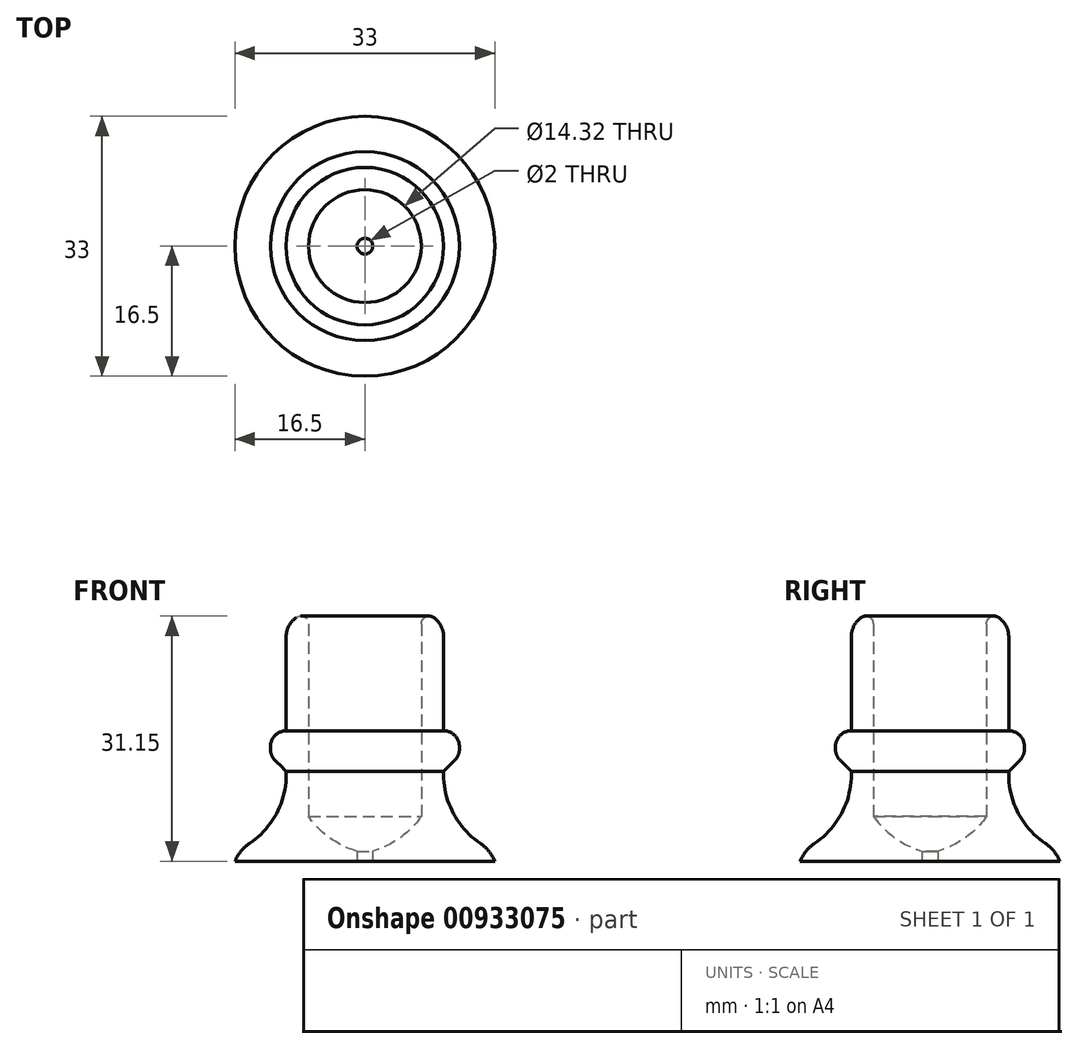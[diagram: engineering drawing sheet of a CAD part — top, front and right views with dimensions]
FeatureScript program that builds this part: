
annotation { "Feature Type Name" : "Feature", "Feature Type Description" : "" }
export const myFeature = defineFeature(function(context is Context, id is Id, definition is map)
    precondition{}
    {
        {
            var Q0;
            Q0=qCreatedBy(makeId("Front.planeOp"),FACE);
            var sketch = newSketch(context, id + "F0", { "sketchPlane" : qUnion([Q0])});
            skLineSegment(sketch, "E0", {"start": v(10, 11.44) * mm, "end": v(12, 13.4) * mm});
            skLineSegment(sketch, "E1", {"start": v(12, 13.4) * mm, "end": v(12, 16.58) * mm});
            skLineSegment(sketch, "E2", {"start": v(0, 0) * mm, "end": v(0, 38.4) * mm, "construction": true});
            skLineSegment(sketch, "E3", {"start": v(12, 16.58) * mm, "end": v(10, 16.58) * mm});
            skLineSegment(sketch, "E4", {"start": v(10, 16.58) * mm, "end": v(10, 31.51) * mm});
            skLineSegment(sketch, "E5", {"start": v(16.5, 0) * mm, "end": v(16.5, 1.28) * mm});
            skArc(sketch, "E6", {"start": v(10, 11.44) * mm, "mid": v(11.66, 5.34) * mm, "end": v(16.5, 1.28) * mm});
            skLineSegment(sketch, "E7", {"start": v(10, 31.51) * mm, "end": v(7.16, 31.51) * mm});
            skLineSegment(sketch, "E8", {"start": v(7.16, 31.51) * mm, "end": v(7.16, 5.7) * mm});
            skLineSegment(sketch, "E9", {"start": v(1, 0.05) * mm, "end": v(1, 1.28) * mm});
            skLineSegment(sketch, "E10", {"start": v(1, 0.05) * mm, "end": v(16.5, 0) * mm});
            skArc(sketch, "E11", {"start": v(1, 1.28) * mm, "mid": v(4.45, 2.97) * mm, "end": v(7.16, 5.7) * mm});
            skSolve(sketch);
        }
        {
            var Q0;
            Q0=makeQuery(id+"F0.imprint","IMPRINT",FACE,{"disambiguationData":[TD([[makeQuery(id+"F0.imprint","IMPRINT",EDGE,{"derivedFrom":sQuery(id+"F0.wireOp",EDGE,"E0")}),1.0]])]});
            var Q1;
            Q1=sQuery(id+"F0.wireOp",EDGE,"E2");
            revolve(context, id + "F1", {"surfaceOperationType" : NewSurfaceOperationType.NEW, "entities" : qUnion([Q0]), "axis" : qUnion([Q1]), "revolveType" : RevolveType.FULL});
        }
        {
            var Q0;
            Q0=makeQuery(id+"F1.opRevolve","SWEPT_EDGE",EDGE,{"disambiguationData":[OSD([sQuery(id+"F0.wireOp",EDGE,"E5"),sQuery(id+"F0.wireOp",EDGE,"E6")])]});
            fillet(context, id + "F2", {"entities" : qUnion([Q0]), "radius" : 5 * mm, "tangentPropagation" : true, "allowEdgeOverflow" : false});
        }
        {
            var Q0;
            Q0=makeQuery(id+"F1.opRevolve","SWEPT_EDGE",EDGE,{"disambiguationData":[OSD([sQuery(id+"F0.wireOp",EDGE,"E0"),sQuery(id+"F0.wireOp",EDGE,"E1")])]});
            fillet(context, id + "F3", {"entities" : qUnion([Q0]), "radius" : 2 * mm, "tangentPropagation" : true, "allowEdgeOverflow" : false});
        }
        {
            var Q0;
            Q0=makeQuery(id+"F1.opRevolve","SWEPT_EDGE",EDGE,{"disambiguationData":[OSD([sQuery(id+"F0.wireOp",EDGE,"E1"),sQuery(id+"F0.wireOp",EDGE,"E3")])]});
            fillet(context, id + "F4", {"entities" : qUnion([Q0]), "radius" : 2 * mm, "tangentPropagation" : true, "allowEdgeOverflow" : false});
        }
        {
            var Q0;
            Q0=makeQuery(id+"F1.opRevolve","SWEPT_EDGE",EDGE,{"disambiguationData":[OSD([sQuery(id+"F0.wireOp",EDGE,"E4"),sQuery(id+"F0.wireOp",EDGE,"E7")])]});
            fillet(context, id + "F5", {"entities" : qUnion([Q0]), "radius" : 3 * mm, "tangentPropagation" : true, "allowEdgeOverflow" : false});
        }
        {
            var Q0;
            Q0=makeQuery(id+"F5.opFillet","BLEND_EDGE",EDGE,{"blendedFrom":[makeQuery(id+"F1.opRevolve","SWEPT_EDGE",EDGE,{"disambiguationData":[OSD([sQuery(id+"F0.wireOp",EDGE,"E4"),sQuery(id+"F0.wireOp",EDGE,"E7")])]}),makeQuery(id+"F1.opRevolve","SWEPT_FACE",FACE,{"disambiguationData":[OSD([sQuery(id+"F0.wireOp",EDGE,"E8")])]})],"blendedInto":[makeQuery(id+"F1.opRevolve","SWEPT_FACE",FACE,{"disambiguationData":[OSD([sQuery(id+"F0.wireOp",EDGE,"E8")])]})]});
            fillet(context, id + "F6", {"entities" : qUnion([Q0]), "radius" : 1 * mm, "tangentPropagation" : true, "allowEdgeOverflow" : false});
        }
    });
